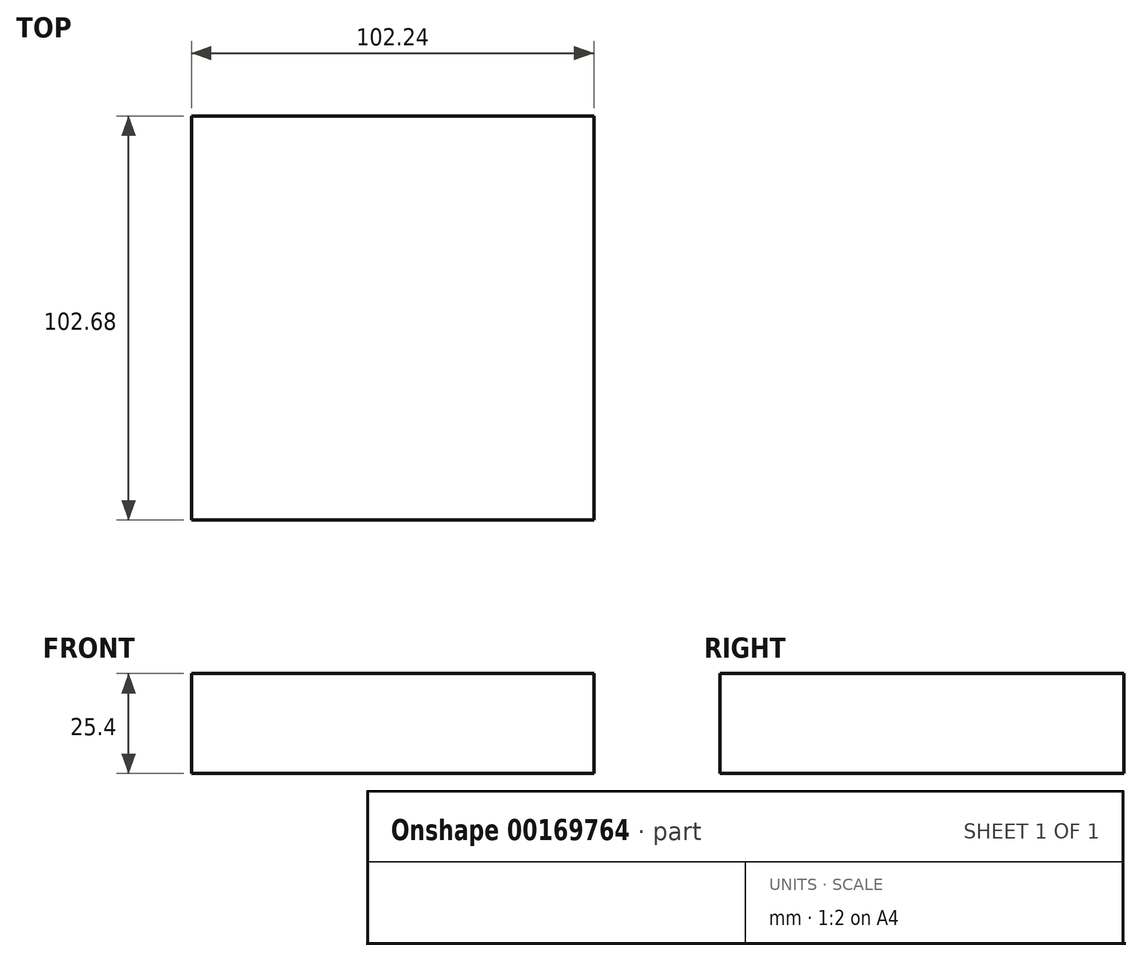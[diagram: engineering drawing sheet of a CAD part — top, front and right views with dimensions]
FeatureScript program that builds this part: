
annotation { "Feature Type Name" : "Feature", "Feature Type Description" : "" }
export const myFeature = defineFeature(function(context is Context, id is Id, definition is map)
    precondition{}
    {
        {
            var Q0;
            Q0=qCreatedBy(makeId("Top.planeOp"),FACE);
            var sketch = newSketch(context, id + "F0", { "sketchPlane" : qUnion([Q0])});
            skLineSegment(sketch, "E0.bottom", {"start": v(-44.26, 54.1) * mm, "end": v(57.98, 54.1) * mm});
            skLineSegment(sketch, "E0.top", {"start": v(-44.26, -48.59) * mm, "end": v(57.98, -48.59) * mm});
            skLineSegment(sketch, "E0.left", {"start": v(-44.26, 54.1) * mm, "end": v(-44.26, -48.59) * mm});
            skLineSegment(sketch, "E0.right", {"start": v(57.98, 54.1) * mm, "end": v(57.98, -48.59) * mm});
            skSolve(sketch);
        }
        {
            var Q0;
            Q0=makeQuery(id+"F0.imprint","IMPRINT",FACE,{"disambiguationData":[TD([[makeQuery(id+"F0.imprint","IMPRINT",EDGE,{"derivedFrom":sQuery(id+"F0.wireOp",EDGE,"E0.bottom")}),-1.0]])]});
            extrude(context, id + "F1", {"entities" : qUnion([Q0]), "depth" : 25.4 * mm});
        }
    });
